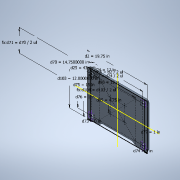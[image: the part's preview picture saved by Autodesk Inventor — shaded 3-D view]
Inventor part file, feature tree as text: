
AUTODESK INVENTOR PART (.ipt)
format: ipt  version: 2020.3 (Build 243373000, 373)  size: 251,904 bytes
history: native  units: in
note: dims shown in document units (in); Inventor stores cm internally (conversion verified against a paired STEP export)
features: hole x4, extrude x2, fillet x2, sketch x2, chamfer x1, projected_geometry x1
ambient origin geometry x8: Origin, YZ Plane, XZ Plane, XY Plane, X Axis, Y Axis, Z Axis, Center Point
bodies: Solid1 (feature_tree)
feature tree (12):
  extrude  "Extrusion1"  Depth=0.625in TaperAngle=0.0deg
  hole  "Hole2"  [1 undecoded]
  hole  "Hole3"  [1 undecoded]
  hole  "Hole5"  [1 undecoded]
  extrude  "Extrusion5"  Depth=0.395in
  chamfer  "Chamfer3"  Distance=8.5in
  fillet  "Fillet4"  [1 undecoded]
  fillet  "Fillet6"  [1 undecoded]
  hole  "Hole6"  [1 undecoded]
  sketch  "Sketch3"  dims[d2=19.75in d4=0.625in d5=0.0in]
  projected_geometry  "Projected Loop1"
  sketch  "Sketch4"  dims[d24=17.0in d25=1.6929in d26=0.163in d27=0.394in d28=0.375in d29=0.25in d30=0.5635in d31=0.559in d32=0.8108in d33=1.2992in d34=0.394in d35=0.375in d36=0.25in d37=0.5635in d38=0.559in d39=0.8108in d66=9.875in d70=14.75in d71=7.375in d72=8.5in d73=0.0in d74=0.0in d75=15.0in d76=1.0in d77=1.0in d80=0.75in d85=4.75in d86=12.0in d87=0.26in d88=0.394in d89=0.496in d90=0.25in d91=90.0deg d92=0.559in d93=0.8108in d94=0.875in d95=12.0in d96=1.0in d97=0.0in d98=0.875in d99=0.125in d100=45.0deg d101=0.75in d103=12.0in d104=6.0in d105=3.5in d106=3.5in d107=0.547in d108=0.75in d109=1.125in d110=0.395in d111=0.5635in d112=1.0in d113=0.8108in d114=3.5in d115=3.5in]
note: 6 required parameter values undecoded (feature->parameter linkage not recoverable at this tier; creation-order binding heuristic only, values carry confidence <= 0.55)
